# Revit family: AGSRTFT
name_source: partatom
category: Electrical Fixtures
units: mm (PartAtom-declared; Revit-internal decimal feet)

## family parameters
Always vertical = Yes
Cut with Voids When Loaded = No
Maintain Annotation Orientation = No
Part Type = Normal
Room Calculation Point = No
Round Connector Dimension = Use Diameter
Shared = No
Work Plane-Based = No

## types (11) — shared parameters
Audible Alarm Buzzer dB = >70dB @ 3.28ft (1m). Quiet conditions.
DC Power = 12-32 VDC - Nominal 24 VDC
Default Elevation = 0.00"
Housing Material = ABS Polylac - PA765
Internal Fuse = None
MAIN BODY 1 = Yes
MAIN BODY 2 = Yes
Manufacturer = American Gas Safety LLC
Operating Temperature = -10 ~ 50°C / 14 ~ 122°F 30 ~ 80% RH (non-condensing)
PANNEL BODY = PANNEL BODY
Power Consumptions = 90mA Max @ 24vdc
Relay = Volt Free (Normally Closed / Common / Normally Open)
1x 30vdc 2A (Non-Latching)
Size: (H x W x D) = 5.51 x 3.74 x 1.18” (140 x 95 x 30mm)
Target Gases = R410A or R32 or R134A
Tel = (727) 608-4375
Weight = Max. 1.77oz (0.05kg)

## per-type parameters (varying)
| type | Altitude Rating | Display | R1234YF | R1234ZE | R134A | R32 | R404A | R407C | R410A | R452B | R454A | R454B | R454C | Storage | Typical |
| R1234YF |  |  | Yes | No | No | No | No | No | No | No | No | No | No |  |  |
| R1234ZE |  |  | No | Yes | No | No | No | No | No | No | No | No | No |  |  |
| R134A |  |  | No | No | Yes | No | No | No | No | No | No | No | No |  |  |
| R32 |  |  | No | No | No | Yes | No | No | No | No | No | No | No |  |  |
| R404A |  |  | No | No | No | No | Yes | No | No | No | No | No | No |  |  |
| R407C |  |  | No | No | No | No | No | Yes | No | No | No | No | No |  |  |
| R410A |  |  | No | No | No | No | No | No | Yes | No | No | No | No |  |  |
| R452B |  |  | No | No | No | No | No | No | No | Yes | No | No | No |  |  |
| R454A |  |  | No | No | No | No | No | No | No | No | Yes | No | No |  |  |
| R454B |  |  | No | No | No | No | No | No | No | No | No | Yes | No |  |  |
| R454C | 2000m | 1.8” TFT | No | No | No | No | No | No | No | No | No | No | Yes | -25 ~ 50°C / -13~122F° up to 95% RH (non-condensing) | #15AWG Power Pair; #18AWG Data Pair-Tinned copper. |

note: column(s) folded — value = type name in every type: Model

## geometry (parser evidence)
native form markers: Sweep x61
no freeform markers — native parametric forms only
